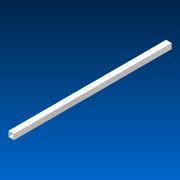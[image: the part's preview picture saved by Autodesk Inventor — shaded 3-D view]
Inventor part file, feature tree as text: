
AUTODESK INVENTOR PART (.ipt)
format: ipt  version: 2022.2 (Build 262287000, 287)  size: 765,952 bytes
history: native  units: in
note: dims shown in document units (in); Inventor stores cm internally (conversion verified against a paired STEP export)
features: other x29, extrude x1, pattern_linear x1, sketch x1, pattern_circular x1
ambient origin geometry x8: Origin, YZ Plane, XZ Plane, XY Plane, X Axis, Y Axis, Z Axis, Center Point
bodies: Solid1 (feature_tree)
feature tree (33):
  extrude  "Extrusion1"  Depth=1.0in
  other  "Work Axis1"
  pattern_linear  "Rectangular Pattern1"  Spacing1=0.0in  [1 undecoded]
  sketch  "Sketch1"  dims[d0=1.0in d1=30.0in d2=0.0in d3=11.4173in d5=1.0in]
  other  "Work Axis2"
  other  "Work Axis3"
  other  "Work Axis4"
  other  "Work Axis5"
  other  "Work Axis6"
  other  "Work Axis7"
  other  "Work Axis8"
  other  "Work Axis9"
  other  "Work Axis10"
  other  "Work Axis11"
  other  "Work Axis12"
  other  "Work Axis13"
  other  "Work Axis14"
  other  "Work Axis15"
  other  "Work Axis16"
  other  "Work Axis17"
  other  "Work Axis18"
  other  "Work Axis19"
  other  "Work Axis20"
  other  "Work Axis21"
  other  "Work Axis22"
  other  "Work Axis23"
  other  "Work Axis24"
  other  "Work Axis25"
  other  "Work Axis26"
  other  "Work Axis27"
  other  "Work Axis28"
  other  "Work Axis29"
  pattern_circular  "CirPattern2"
note: 1 required parameter value undecoded (feature->parameter linkage not recoverable at this tier; creation-order binding heuristic only, values carry confidence <= 0.55)
